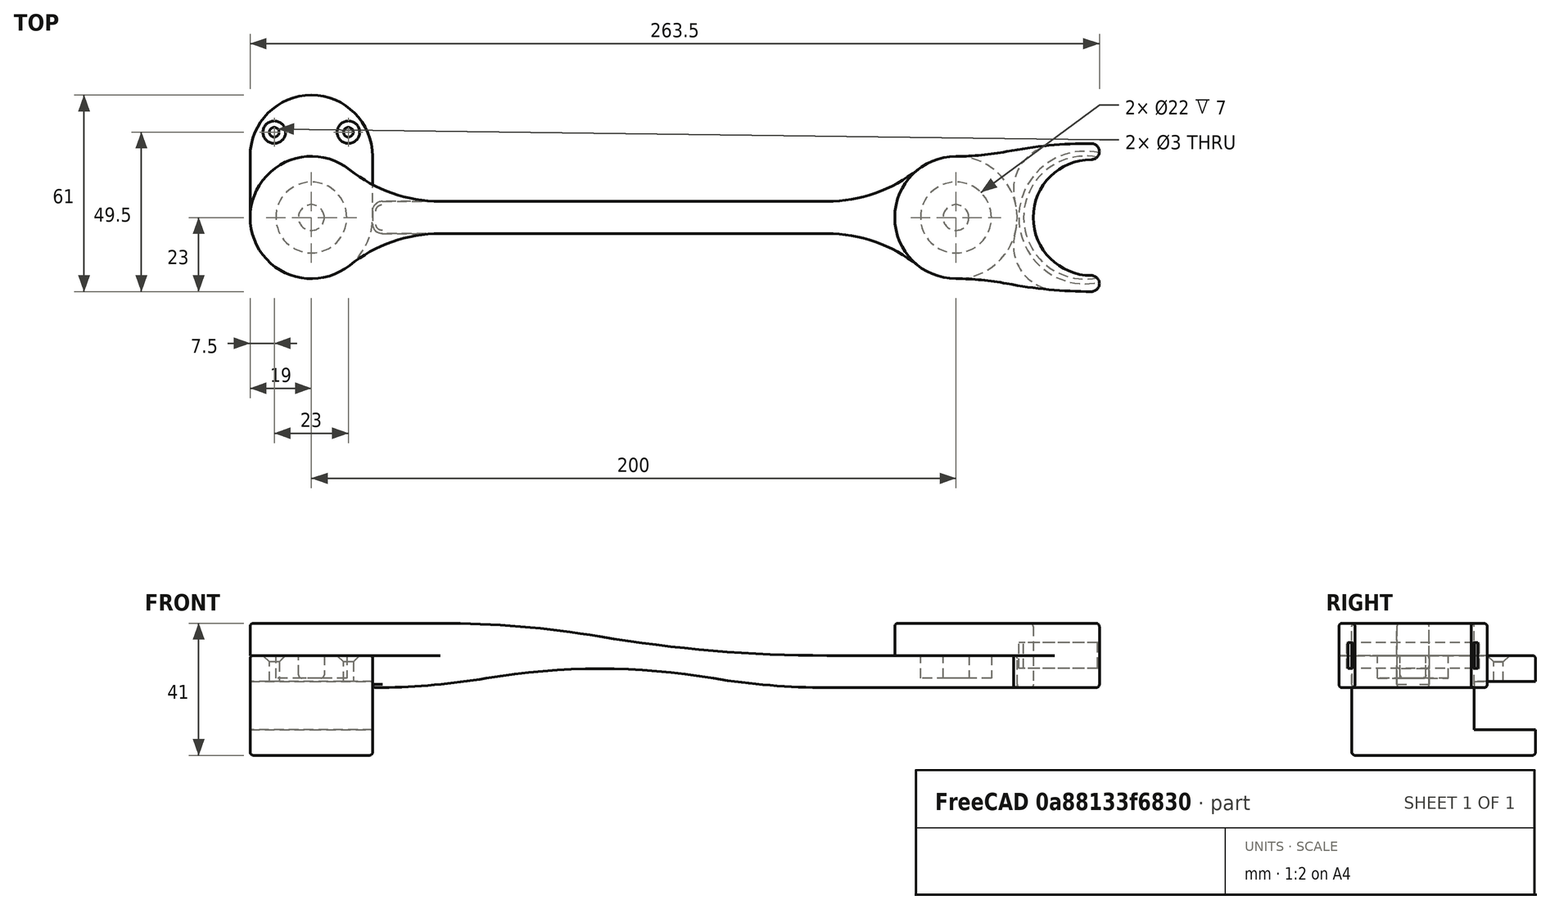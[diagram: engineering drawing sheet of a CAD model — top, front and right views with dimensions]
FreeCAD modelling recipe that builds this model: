
FCSTD DOCUMENT  (FreeCAD 0.21R33771 (Git))
Label: MicroscopeArm
License: All rights reserved
LicenseURL: http://en.wikipedia.org/wiki/All_rights_reserved
objects: Sketcher::SketchObject×13, PartDesign::Pad×7, PartDesign::Pocket×7, PartDesign::Fillet×6, PartDesign::Body×3, App::Part×3, Mesh::Feature×3, PartDesign::SubShapeBinder×2, Spreadsheet::Sheet×1
note: 58 computed .brp shape members not serialized (recipe doc carries the construction recipe); baked Part::Feature solids carry a one-line shape summary decoded from their .brp

FEATURE [Spreadsheet::Sheet] Spreadsheet
  cells = A1='HalfArmLength; B1(HalfArmLength)=200; A2='BearingOuterDiameter; B2(BearingOuterDiameter)=22; A3='BearingInnerDiameter; B3(BearingInnerDiameter)=8; A4='TableThickness; B4(TableThickness)=15; A5='Wall; B5(Wall)=8; A6='BearingThickness; B6(BearingThickness)=7; A7='ScrewHeadDiameter; B7(ScrewHeadDiameter)=7; A8='ScrewDiameter; B8(ScrewDiameter)=3; A9='ArmThickness; B9(ArmThickness)=38; A10='ArmThinness; B10(ArmThinness)=10; A11='ArmTransitionSize; B11(ArmTransitionSize)=40; A12='MicroscopeDiameter; B12(MicroscopeDiameter)=36
FEATURE [Sketcher::SketchObject] Sketch  label="TableAttachmentTopSketch"
  FullyConstrained = true
  MapMode = 5
  Support = -> [XY_Plane001]
  expr: Constraints[2] = Spreadsheet.Wall * 2 + Spreadsheet.BearingOuterDiameter
  expr: Constraints[8] = Spreadsheet.Wall + Spreadsheet.BearingOuterDiameter / 2
  sketch-geometry (5):
    g0: ArcOfCircle CenterX=0 CenterY=0 CenterZ=0 NormalX=0 NormalY=0 NormalZ=1 AngleXU=0 Radius=19 StartAngle=3.14159 EndAngle=6.28319
    g1: LineSegment StartX=-19 StartY=2.3e-15 StartZ=0 EndX=-19 EndY=19 EndZ=0
    g2: LineSegment StartX=19 StartY=-4.7e-15 StartZ=0 EndX=19 EndY=19 EndZ=0
    g3: LineSegment StartX=-19 StartY=19 StartZ=0 EndX=0 EndY=19 EndZ=0
    g4: ArcOfCircle CenterX=1.1e-15 CenterY=19 CenterZ=0 NormalX=0 NormalY=0 NormalZ=1 AngleXU=0 Radius=19 StartAngle=0 EndAngle=3.14159
  constraints (15):
    c: PointOnObject(g0,g-1)
    c: PointOnObject(g0,g-1)
    c: Diameter(g0) = 38
    c: Coincident(g1,g0)
    c: Vertical(g1)
    c: Coincident(g2,g0)
    c: Vertical(g2)
    c: Horizontal(g1,g2)
    c: DistanceY(g1,g1) = 19
    c: Coincident(g3,g1)
    c: Horizontal(g3)
    c: Coincident(g4,g3)
    c: Coincident(g4,g1)
    c: Coincident(g4,g2)
    c: Coincident(g0,g-1)
FEATURE [PartDesign::Pad] Pad  label="TableAttachmentTopPad"
  Direction = (0,0,1)
  Length = 31
  Length2 = 10
  Profile = -> Sketch
  ReferenceAxis = -> Sketch [N_Axis]
  Type = 0
  expr: Length = Spreadsheet.TableThickness + 2 * Spreadsheet.Wall
FEATURE [Sketcher::SketchObject] Sketch001  label="TableCutSketch"
  ExternalGeometry = -> [Pad]
  FullyConstrained = true
  MapMode = 5
  Placement = pos=(0,0,0) rot=(0.57735,0.57735,0.57735;2.0944rad)
  Support = -> [YZ_Plane001]
  expr: Constraints[8] = Spreadsheet.TableThickness
  expr: Constraints[9] = Spreadsheet.Wall
  sketch-geometry (4):
    g0: LineSegment StartX=38 StartY=23 StartZ=0 EndX=19 EndY=23 EndZ=0
    g1: LineSegment StartX=19 StartY=23 StartZ=0 EndX=19 EndY=8 EndZ=0
    g2: LineSegment StartX=19 StartY=8 StartZ=0 EndX=38 EndY=8 EndZ=0
    g3: LineSegment StartX=38 StartY=8 StartZ=0 EndX=38 EndY=23 EndZ=0
  constraints (12):
    c: Coincident(g0,g1)
    c: Coincident(g1,g2)
    c: Coincident(g2,g3)
    c: Coincident(g3,g0)
    c: Horizontal(g0)
    c: Horizontal(g2)
    c: Vertical(g1)
    c: Vertical(g3)
    c: DistanceY(g3,g3) = 15
    c: DistanceY(g-1,g2) = 8
    c: Vertical(g0,g-3)
    c: Vertical(g-3,g0)
FEATURE [PartDesign::Pocket] Pocket  label="TableCut"
  BaseFeature = -> Pad
  Direction = (-1,2e-16,-3e-16)
  Length = 38
  Length2 = 5
  Midplane = true
  Profile = -> Sketch001
  ReferenceAxis = -> Sketch001 [N_Axis]
  Type = 0
  expr: Length = Spreadsheet.BearingOuterDiameter + 2 * Spreadsheet.Wall
FEATURE [Sketcher::SketchObject] Sketch002  label="BearingPocketSketch"
  FullyConstrained = true
  MapMode = 5
  Placement = pos=(0,0,31) rot=(0,0,1;0rad)
  Support = -> [Pocket]
  expr: Constraints[1] = Spreadsheet.BearingOuterDiameter
  sketch-geometry (1):
    g0: Circle CenterX=0 CenterY=0 CenterZ=0 NormalX=0 NormalY=0 NormalZ=1 AngleXU=0 Radius=11
  constraints (2):
    c: Coincident(g0,g-1)
    c: Diameter(g0) = 22
FEATURE [PartDesign::Pocket] Pocket001  label="BearingPocket"
  BaseFeature = -> Pocket
  Direction = (0,0,-1)
  Length = 7
  Length2 = 5
  Profile = -> Sketch002
  ReferenceAxis = -> Sketch002 [N_Axis]
  Type = 0
  expr: Length = Spreadsheet.BearingThickness
FEATURE [Sketcher::SketchObject] Sketch003  label="ScrewHeadPocketSketch"
  ExternalGeometry = -> [Pocket001]
  FullyConstrained = true
  MapMode = 5
  Placement = pos=(0,0,31) rot=(0,0,1;0rad)
  Support = -> [Pocket001]
  expr: Constraints[11] = Spreadsheet.ScrewHeadDiameter / 2 + Spreadsheet.Wall / 2
  expr: Constraints[8] = Spreadsheet.ScrewHeadDiameter
  expr: Constraints[9] = Spreadsheet.ScrewHeadDiameter / 2 + Spreadsheet.Wall / 2
  sketch-geometry (5):
    g0: Circle CenterX=-11.5 CenterY=26.5 CenterZ=0 NormalX=0 NormalY=0 NormalZ=1 AngleXU=0 Radius=3.5
    g1: Circle CenterX=11.5 CenterY=26.5 CenterZ=0 NormalX=0 NormalY=0 NormalZ=1 AngleXU=0 Radius=3.5
    g2: LineSegment StartX=-19 StartY=19 StartZ=0 EndX=19 EndY=19 EndZ=0
    g3: LineSegment StartX=-11.5 StartY=26.5 StartZ=0 EndX=1.8e-15 EndY=19 EndZ=0
    g4: LineSegment StartX=1.8e-15 StartY=19 StartZ=0 EndX=11.5 EndY=26.5 EndZ=0
  constraints (12):
    c: Coincident(g2,g-3)
    c: Coincident(g2,g-3)
    c: Equal(g1,g0)
    c: Coincident(g3,g0)
    c: Coincident(g3,g-3)
    c: Coincident(g4,g3)
    c: Coincident(g4,g1)
    c: Equal(g3,g4)
    c: Diameter(g0) = 7
    c: DistanceX(g1,g2) = 7.5
    c: Horizontal(g1,g0)
    c: DistanceY(g2,g1) = 7.5
FEATURE [PartDesign::Pocket] Pocket002  label="ScrewHeadPocket"
  BaseFeature = -> Pocket001
  Direction = (0,0,-1)
  Length = 2
  Length2 = 5
  Profile = -> Sketch003
  ReferenceAxis = -> Sketch003 [N_Axis]
  TaperAngle = -45
  Type = 0
  expr: Length = (Spreadsheet.ScrewHeadDiameter - Spreadsheet.ScrewDiameter) / 2
FEATURE [PartDesign::Pocket] Pocket003  label="ScrewPocket"
  BaseFeature = -> Pocket002
  Direction = (0,0,-1)
  Length = 6
  Length2 = 5
  Profile = -> Pocket002 [Edge31,Edge29]
  Type = 0
  expr: Length = Spreadsheet.Wall - (Spreadsheet.ScrewHeadDiameter - Spreadsheet.ScrewDiameter) / 2
FEATURE [PartDesign::Fillet] Fillet
  Base = -> Pocket003 [Face4]
  BaseFeature = -> Pocket003
  Radius = 1
  SupportTransform = false
  UseAllEdges = false
FEATURE [PartDesign::Fillet] Fillet001
  Base = -> Fillet [Edge3,Edge6,Edge14,Edge13]
  BaseFeature = -> Fillet
  Radius = 1
  SupportTransform = false
  UseAllEdges = false
FEATURE [PartDesign::Body] Body  label="TableAttachmentBody"
  Group = -> [Sketch,Pad,Sketch001,Pocket,Sketch002,Pocket001,Sketch003,Pocket002,Pocket003,Fillet,Fillet001]
  Origin = -> Origin001
  Tip = -> Fillet001
FEATURE [App::Part] Part  label="TableAttachment"
  Group = -> [Body]
  Origin = -> Origin
FEATURE [Mesh::Feature] Mesh  label="TableAttachment (Meshed)"
FEATURE [PartDesign::SubShapeBinder] Binder  label="TableAttachmentBearingPocketSketchBinder"
  BindCopyOnChange = 0
  BindMode = 0
  ClaimChildren = false
  Context = -> Part001 [Body001.Binder.]
  Fuse = false
  MakeFace = true
  OffsetFill = false
  OffsetIntersection = false
  OffsetJoinType = 0
  OffsetOpenResult = false
  PartialLoad = false
  Relative = true
  Support = -> [Part[Body.Pocket001.Sketch002.]]
  _Version = 2
FEATURE [Sketcher::SketchObject] Sketch004  label="ArmTopSketch"
  ExternalGeometry = -> [Binder]
  FullyConstrained = true
  MapMode = 5
  Placement = pos=(0,0,31) rot=(0,0,1;0rad)
  Support = -> [Binder]
  expr: Constraints[10] = <<Spreadsheet>>.ArmThinness
  expr: Constraints[11] = <<Spreadsheet>>.ArmTransitionSize
  expr: Constraints[15] = <<Spreadsheet>>.HalfArmLength - <<Spreadsheet>>.ArmThickness / 2
  expr: Constraints[1] = <<Spreadsheet>>.ArmThickness
  sketch-geometry (6):
    g0: ArcOfCircle CenterX=0 CenterY=0 CenterZ=0 NormalX=0 NormalY=0 NormalZ=1 AngleXU=0 Radius=19 StartAngle=0.897447 EndAngle=5.38574
    g1: LineSegment StartX=40 StartY=5 StartZ=0 EndX=181 EndY=5 EndZ=0
    g2: ArcOfCircle CenterX=40 CenterY=50.1429 CenterZ=0 NormalX=0 NormalY=0 NormalZ=1 AngleXU=0 Radius=45.1429 StartAngle=4.03904 EndAngle=4.71239
    g3: LineSegment StartX=40 StartY=-5 StartZ=0 EndX=181 EndY=-5 EndZ=0
    g4: ArcOfCircle CenterX=40 CenterY=-50.1429 CenterZ=0 NormalX=0 NormalY=0 NormalZ=1 AngleXU=0 Radius=45.1429 StartAngle=1.5708 EndAngle=2.24415
    g5: LineSegment StartX=181 StartY=5 StartZ=0 EndX=181 EndY=-5 EndZ=0
  constraints (16):
    c: Coincident(g0,g-3)
    c: Diameter(g0) = 38
    c: Vertical(g0,g0)
    c: Horizontal(g1)
    c: Tangent(g2,g1) = -1.5708
    c: Tangent(g2,g0) = 1.5708
    c: Horizontal(g3)
    c: Vertical(g1,g3)
    c: Tangent(g4,g3) = 1.5708
    c: Tangent(g4,g0) = 1.5708
    c: DistanceY(g3,g1) = 10
    c: DistanceX(g0,g1) = 40
    c: Vertical(g5)
    c: Coincident(g3,g5)
    c: Coincident(g1,g5)
    c: DistanceX(g0,g3) = 181
FEATURE [PartDesign::Pad] Pad001  label="ArmTopPad"
  Direction = (0,0,1)
  Length = 10
  Length2 = 10
  Profile = -> Sketch004
  ReferenceAxis = -> Sketch004 [N_Axis]
  Refine = true
  Type = 0
  expr: Length = <<Spreadsheet>>.ArmThinness
FEATURE [Sketcher::SketchObject] Sketch005  label="ArmUnderSketch"
  FullyConstrained = true
  MapMode = 5
  Placement = pos=(0,0,31) rot=(1,0,0;3.14159rad)
  Support = -> [Pad001]
  expr: Constraints[10] = <<Spreadsheet>>.HalfArmLength
  expr: Constraints[12] = <<Spreadsheet>>.ArmTransitionSize
  expr: Constraints[4] = <<Spreadsheet>>.ArmThinness
  expr: Constraints[5] = <<Spreadsheet>>.ArmThickness / 2
  expr: Constraints[9] = <<Spreadsheet>>.ArmThickness
  sketch-geometry (6):
    g0: LineSegment StartX=19 StartY=5 StartZ=0 EndX=160 EndY=5 EndZ=0
    g1: LineSegment StartX=160 StartY=-5 StartZ=0 EndX=19 EndY=-5 EndZ=0
    g2: LineSegment StartX=19 StartY=-5 StartZ=0 EndX=19 EndY=5 EndZ=0
    g3: ArcOfCircle CenterX=200 CenterY=0 CenterZ=0 NormalX=0 NormalY=0 NormalZ=1 AngleXU=0 Radius=19 StartAngle=4.03904 EndAngle=8.52733
    g4: ArcOfCircle CenterX=160 CenterY=50.1429 CenterZ=0 NormalX=0 NormalY=0 NormalZ=1 AngleXU=0 Radius=45.1429 StartAngle=4.71239 EndAngle=5.38574
    g5: ArcOfCircle CenterX=160 CenterY=-50.1429 CenterZ=0 NormalX=0 NormalY=0 NormalZ=1 AngleXU=0 Radius=45.1429 StartAngle=0.897447 EndAngle=1.5708
  constraints (16):
    c: Coincident(g1,g2)
    c: Coincident(g2,g0)
    c: Horizontal(g0)
    c: Horizontal(g1)
    c: DistanceY(g2,g2) = 10
    c: DistanceX(g-1,g0) = 19
    c: Symmetric(g0,g1,g-1)
    c: PointOnObject(g3,g-1)
    c: Vertical(g3,g3)
    c: Diameter(g3) = 38
    c: DistanceX(g-1,g3) = 200
    c: Tangent(g4,g3) = 1.5708
    c: DistanceX(g4,g3) = 40
    c: Tangent(g5,g3) = 1.5708
    c: Tangent(g5,g1) = -1.5708
    c: Tangent(g0,g4) = -1.5708
FEATURE [PartDesign::Pad] Pad002  label="ArmUnderPad"
  BaseFeature = -> Pad001
  Direction = (0,0,-1)
  Length = 10
  Length2 = 10
  Profile = -> Sketch005
  ReferenceAxis = -> Sketch005 [N_Axis]
  Refine = true
  Type = 0
  expr: Length = <<Spreadsheet>>.ArmThinness
FEATURE [Sketcher::SketchObject] Sketch006
  ExternalGeometry = -> [Pad002]
  FullyConstrained = true
  MapMode = 5
  Placement = pos=(0,0,31) rot=(0,0,1;0rad)
  Support = -> [Pad002]
  expr: Constraints[1] = <<Spreadsheet>>.BearingOuterDiameter
  sketch-geometry (1):
    g0: Circle CenterX=200 CenterY=0 CenterZ=0 NormalX=0 NormalY=0 NormalZ=1 AngleXU=0 Radius=11
  constraints (2):
    c: Coincident(g0,g-3)
    c: Diameter(g0) = 22
FEATURE [PartDesign::Pocket] Pocket004
  BaseFeature = -> Pad002
  Direction = (0,0,-1)
  Length = 7
  Length2 = 5
  Profile = -> Sketch006
  ReferenceAxis = -> Sketch006 [N_Axis]
  Type = 0
  expr: Length = <<Spreadsheet>>.BearingThickness
FEATURE [Sketcher::SketchObject] Sketch007  label="BearingPegSketch"
  ExternalGeometry = -> [Pocket004]
  FullyConstrained = true
  MapMode = 5
  Placement = pos=(0,0,31) rot=(1,0,0;3.14159rad)
  Support = -> [Pocket004]
  expr: Constraints[1] = <<Spreadsheet>>.BearingInnerDiameter
  sketch-geometry (1):
    g0: Circle CenterX=0 CenterY=0 CenterZ=0 NormalX=0 NormalY=0 NormalZ=1 AngleXU=0 Radius=4
  constraints (2):
    c: Coincident(g0,g-3)
    c: Diameter(g0) = 8
FEATURE [PartDesign::Pad] Pad003  label="BearingPeg"
  BaseFeature = -> Pocket004
  Direction = (0,0,-1)
  Length = 7
  Length2 = 10
  Profile = -> Sketch007
  ReferenceAxis = -> Sketch007 [N_Axis]
  Type = 0
  expr: Length = <<Spreadsheet>>.BearingThickness
FEATURE [Sketcher::SketchObject] Sketch008  label="ArchSketch"
  ExternalGeometry = -> [Pad003]
  FullyConstrained = true
  MapMode = 5
  Placement = pos=(0,-5,1.7e-15) rot=(1,0,0;1.5708rad)
  Support = -> [Pad003]
  expr: Constraints[15] = <<Spreadsheet>>.ArmThinness
  sketch-geometry (11):
    g0: GeomPoint X=89.5 Y=21 Z=0
    g1: ArcOfCircle CenterX=40 CenterY=-258.063 CenterZ=0 NormalX=0 NormalY=0 NormalZ=1 AngleXU=0 Radius=299.063 StartAngle=1.40451 EndAngle=1.5708
    g2: ArcOfCircle CenterX=160 CenterY=456.938 CenterZ=0 NormalX=0 NormalY=0 NormalZ=1 AngleXU=0 Radius=425.938 StartAngle=4.54611 EndAngle=4.71239
    g3: LineSegment StartX=160 StartY=31 StartZ=0 EndX=188.151 EndY=31 EndZ=0
    g4: LineSegment StartX=188.151 StartY=31 StartZ=0 EndX=188.151 EndY=41 EndZ=0
    g5: LineSegment StartX=188.151 StartY=41 StartZ=0 EndX=40 EndY=41 EndZ=0
    g6: ArcOfCircle CenterX=19 CenterY=233.969 CenterZ=0 NormalX=0 NormalY=0 NormalZ=1 AngleXU=0 Radius=212.969 StartAngle=4.71239 EndAngle=4.87867
    g7: ArcOfCircle CenterX=89.5 CenterY=-186.094 CenterZ=0 NormalX=0 NormalY=0 NormalZ=1 AngleXU=0 Radius=212.969 StartAngle=1.40451 EndAngle=1.73708
    g8: ArcOfCircle CenterX=160 CenterY=233.969 CenterZ=0 NormalX=0 NormalY=0 NormalZ=1 AngleXU=0 Radius=212.969 StartAngle=4.54611 EndAngle=4.71239
    g9: GeomPoint X=89.5 Y=26.875 Z=0
    g10: LineSegment StartX=19 StartY=21 StartZ=0 EndX=160 EndY=21 EndZ=0
  constraints (25):
    c: Tangent(g2,g-4) = -1.5708
    c: Tangent(g2,g1) = 1.5708
    c: Coincident(g3,g2)
    c: Coincident(g3,g-4)
    c: Vertical(g4)
    c: Coincident(g5,g4)
    c: Horizontal(g5)
    c: Tangent(g1,g-3) = -1.5708
    c: Coincident(g4,g3)
    c: Coincident(g5,g1)
    c: Vertical(g1,g0)
    c: Horizontal(g6,g7)
    c: Tangent(g7,g6) = 1.5708
    c: Tangent(g8,g7) = 1.5708
    c: PointOnObject(g9,g7)
    c: DistanceY(g9,g1) = 10
    c: Symmetric(g9,g8,g7)
    c: Coincident(g10,g6)
    c: Coincident(g10,g8)
    c: Horizontal(g10)
    c: Symmetric(g6,g8,g0)
    c: Vertical(g2,g8)
    c: Vertical(g9,g0)
    c: Coincident(g-5,g6)
    c: Vertical(g7,g0)
FEATURE [PartDesign::Pocket] Pocket005  label="ArchPocket"
  BaseFeature = -> Pad003
  Direction = (0,1,-4e-16)
  Length = 5
  Length2 = 5
  Profile = -> Sketch008
  ReferenceAxis = -> Sketch008 [N_Axis]
  Refine = true
  Type = 1
FEATURE [PartDesign::Fillet] Fillet002  label="BearingPegFillet"
  Base = -> Pocket005 [Edge40]
  BaseFeature = -> Pocket005
  Radius = 1
  SupportTransform = false
  UseAllEdges = false
FEATURE [PartDesign::Fillet] Fillet003  label="EndOfArchFillet"
  Base = -> Fillet002 [Edge17,Edge26]
  BaseFeature = -> Fillet002
  Radius = 3
  SupportTransform = false
  UseAllEdges = false
FEATURE [PartDesign::Fillet] Fillet004  label="TopAndBottomFillets"
  Base = -> Fillet003 [Edge54,Edge25]
  BaseFeature = -> Fillet003
  Radius = 1
  SupportTransform = false
  UseAllEdges = false
FEATURE [PartDesign::Body] Body001  label="ArmBody"
  Group = -> [Binder,Sketch004,Pad001,Sketch005,Pad002,Sketch006,Pocket004,Sketch007,Pad003,Sketch008,Pocket005,Fillet002,Fillet003,Fillet004]
  Origin = -> Origin003
  Tip = -> Fillet004
FEATURE [App::Part] Part001  label="Arm"
  Group = -> [Body001]
  Origin = -> Origin002
FEATURE [Mesh::Feature] Mesh001  label="Arm (Meshed)"
FEATURE [PartDesign::SubShapeBinder] Binder001  label="ArmUnderSketchBinder"
  BindCopyOnChange = 0
  BindMode = 0
  ClaimChildren = false
  Context = -> Part002 [Body002.Binder001.]
  Fuse = false
  MakeFace = true
  OffsetFill = false
  OffsetIntersection = false
  OffsetJoinType = 0
  OffsetOpenResult = false
  PartialLoad = false
  Relative = true
  Support = -> [Part001[Body001.Pad002.Sketch005.]]
  _Version = 2
FEATURE [Sketcher::SketchObject] Sketch009  label="HolderSketch"
  ExternalGeometry = -> [Binder001]
  FullyConstrained = true
  MapMode = 5
  Placement = pos=(0,0,31) rot=(0,0,1;0rad)
  Support = -> [Binder001]
  expr: Constraints[5] = <<Spreadsheet>>.MicroscopeDiameter
  expr: Constraints[6] = (<<Spreadsheet>>.MicroscopeDiameter + <<Spreadsheet>>.ArmThickness) / 2 + 5
  sketch-geometry (8):
    g0: ArcOfCircle CenterX=200 CenterY=0 CenterZ=0 NormalX=0 NormalY=0 NormalZ=1 AngleXU=0 Radius=19 StartAngle=1.5708 EndAngle=4.71239
    g1: ArcOfCircle CenterX=242 CenterY=0 CenterZ=0 NormalX=0 NormalY=0 NormalZ=1 AngleXU=0 Radius=18 StartAngle=1.5708 EndAngle=4.71239
    g2: ArcOfCircle CenterX=242 CenterY=20.5 CenterZ=0 NormalX=0 NormalY=0 NormalZ=1 AngleXU=0 Radius=2.5 StartAngle=4.71239 EndAngle=7.85398
    g3: ArcOfCircle CenterX=242 CenterY=-116.063 CenterZ=0 NormalX=0 NormalY=0 NormalZ=1 AngleXU=0 Radius=139.063 StartAngle=1.5708 EndAngle=1.7607
    g4: ArcOfCircle CenterX=200 CenterY=102.438 CenterZ=0 NormalX=0 NormalY=0 NormalZ=1 AngleXU=0 Radius=83.4375 StartAngle=4.71239 EndAngle=4.90229
    g5: ArcOfCircle CenterX=200 CenterY=-102.438 CenterZ=0 NormalX=0 NormalY=0 NormalZ=1 AngleXU=0 Radius=83.4375 StartAngle=1.38089 EndAngle=1.5708
    g6: ArcOfCircle CenterX=242 CenterY=116.063 CenterZ=0 NormalX=0 NormalY=0 NormalZ=1 AngleXU=0 Radius=139.063 StartAngle=4.52249 EndAngle=4.71239
    g7: ArcOfCircle CenterX=242 CenterY=-20.5 CenterZ=0 NormalX=0 NormalY=0 NormalZ=1 AngleXU=0 Radius=2.5 StartAngle=4.71239 EndAngle=7.85398
  constraints (23):
    c: Coincident(g0,g-3)
    c: PointOnObject(g0,g-3)
    c: Vertical(g0,g0)
    c: PointOnObject(g1,g-1)
    c: Vertical(g1,g1)
    c: Diameter(g1) = 36
    c: DistanceX(g0,g1) = 42
    c: Vertical(g1,g1)
    c: Vertical(g0,g0)
    c: Tangent(g1,g2) = 1.5708
    c: Tangent(g2,g3) = -1.5708
    c: Tangent(g3,g4) = 1.5708
    c: Tangent(g4,g0) = 1.5708
    c: Vertical(g2,g1)
    c: DistanceY(g1,g2) = 5
    c: Horizontal(g3,g2)
    c: Tangent(g0,g5) = 1.5708
    c: Tangent(g5,g6) = 1.5708
    c: Tangent(g6,g7) = -1.5708
    c: Vertical(g6,g1)
    c: Horizontal(g5,g7)
    c: Tangent(g7,g1) = 1.5708
    c: DistanceY(g6,g1) = 5
FEATURE [PartDesign::Pad] Pad004  label="HolderPad"
  Direction = (0,0,1)
  Length = 10
  Length2 = 10
  Profile = -> Sketch009
  ReferenceAxis = -> Sketch009 [N_Axis]
  Type = 0
  expr: Length = <<Spreadsheet>>.ArmThinness
FEATURE [Sketcher::SketchObject] Sketch010  label="BearingConnectorSketch"
  ExternalGeometry = -> [Pad004]
  FullyConstrained = true
  MapMode = 5
  Placement = pos=(0,0,31) rot=(1,0,0;3.14159rad)
  Support = -> [Pad004]
  expr: Constraints[1] = <<Spreadsheet>>.BearingInnerDiameter
  sketch-geometry (1):
    g0: Circle CenterX=200 CenterY=0 CenterZ=0 NormalX=0 NormalY=0 NormalZ=1 AngleXU=0 Radius=4
  constraints (2):
    c: Coincident(g0,g-3)
    c: Diameter(g0) = 8
FEATURE [PartDesign::Pad] Pad005  label="BearingConnectorPad"
  BaseFeature = -> Pad004
  Direction = (0,0,-1)
  Length = 7
  Length2 = 10
  Profile = -> Sketch010
  ReferenceAxis = -> Sketch010 [N_Axis]
  Type = 0
  expr: Length = <<Spreadsheet>>.BearingThickness
FEATURE [Sketcher::SketchObject] Sketch011  label="StrapSketch"
  AttachmentOffset = pos=(0,0,-10) rot=(0,0,1;0rad)
  ExternalGeometry = -> [Pad005]
  FullyConstrained = true
  MapMode = 5
  Placement = pos=(0,0,31) rot=(0,0,1;0rad)
  Support = -> [Pad005]
  expr: .AttachmentOffset.Base.z = -<<Spreadsheet>>.ArmThinness
  sketch-geometry (6):
    g0: Circle CenterX=240.089 CenterY=0 CenterZ=0 NormalX=0 NormalY=0 NormalZ=1 AngleXU=0 Radius=19.0889
    g1: Circle CenterX=240.089 CenterY=0 CenterZ=0 NormalX=0 NormalY=0 NormalZ=1 AngleXU=0 Radius=20.5889
    g2: GeomPoint X=259.178 Y=0 Z=0
    g3: GeomPoint X=260.678 Y=0 Z=0
    g4: GeomPoint X=221 Y=0 Z=0
    g5: GeomPoint X=224 Y=0 Z=0
  constraints (13):
    c: PointOnObject(g0,g-1)
    c: PointOnObject(g2,g0)
    c: PointOnObject(g3,g1)
    c: PointOnObject(g3,g-1)
    c: PointOnObject(g2,g-1)
    c: DistanceX(g2,g3) = 1.5
    c: PointOnObject(g4,g0)
    c: PointOnObject(g4,g-1)
    c: PointOnObject(g-3,g1)
    c: Coincident(g0,g1)
    c: PointOnObject(g5,g-4)
    c: PointOnObject(g5,g-1)
    c: DistanceX(g4,g5) = 3
FEATURE [Sketcher::SketchObject] Sketch012  label="UndersideSketch"
  ExternalGeometry = -> [Pad005]
  FullyConstrained = true
  MapMode = 5
  Placement = pos=(0,0,31) rot=(1,0,0;3.14159rad)
  Support = -> [Pad005]
  sketch-geometry (8):
    g0: ArcOfCircle CenterX=200 CenterY=0 CenterZ=0 NormalX=0 NormalY=0 NormalZ=1 AngleXU=0 Radius=19 StartAngle=6.01689 EndAngle=6.54948
    g1: ArcOfCircle CenterX=242 CenterY=0 CenterZ=0 NormalX=0 NormalY=0 NormalZ=1 AngleXU=0 Radius=18 StartAngle=1.5708 EndAngle=4.71239
    g2: ArcOfCircle CenterX=242 CenterY=-20.5 CenterZ=0 NormalX=0 NormalY=0 NormalZ=1 AngleXU=0 Radius=2.5 StartAngle=4.71239 EndAngle=7.85398
    g3: ArcOfCircle CenterX=231.757 CenterY=-8.66253 CenterZ=0 NormalX=0 NormalY=0 NormalZ=1 AngleXU=0 Radius=13.9176 StartAngle=2.8753 EndAngle=4.63045
    g4: ArcOfCircle CenterX=231.757 CenterY=8.66253 CenterZ=0 NormalX=0 NormalY=0 NormalZ=1 AngleXU=0 Radius=13.9176 StartAngle=1.65273 EndAngle=3.40789
    g5: ArcOfCircle CenterX=242 CenterY=116.063 CenterZ=0 NormalX=0 NormalY=0 NormalZ=1 AngleXU=0 Radius=139.063 StartAngle=4.63045 EndAngle=4.71239
    g6: ArcOfCircle CenterX=242 CenterY=20.5 CenterZ=0 NormalX=0 NormalY=0 NormalZ=1 AngleXU=0 Radius=2.5 StartAngle=4.71239 EndAngle=7.85398
    g7: ArcOfCircle CenterX=242 CenterY=-116.063 CenterZ=0 NormalX=0 NormalY=0 NormalZ=1 AngleXU=0 Radius=139.063 StartAngle=1.5708 EndAngle=1.65273
  constraints (22):
    c: Equal(g-3,g0)
    c: Coincident(g0,g-3)
    c: Coincident(g5,g-8)
    c: Coincident(g1,g-4)
    c: Coincident(g1,g-5)
    c: Tangent(g4,g-6) = -1.5708
    c: DistanceY(g0,g0) = 10
    c: Vertical(g0,g0)
    c: Tangent(g4,g0) = 1.5708
    c: Tangent(g3,g-8) = -1.5708
    c: Tangent(g3,g0) = 1.5708
    c: Vertical(g1,g1)
    c: Coincident(g2,g1)
    c: Coincident(g-7,g2)
    c: Coincident(g5,g3)
    c: Coincident(g2,g5)
    c: Coincident(g6,g-5)
    c: Coincident(g6,g1)
    c: Vertical(g6,g6)
    c: Coincident(g-6,g7)
    c: Coincident(g7,g4)
    c: Vertical(g7,g6)
FEATURE [PartDesign::Pad] Pad006  label="UndersidePad"
  BaseFeature = -> Pad005
  Direction = (0,0,-1)
  Length = 10
  Length2 = 10
  Profile = -> Sketch012
  ReferenceAxis = -> Sketch012 [N_Axis]
  Refine = true
  Type = 0
  expr: Length = <<Spreadsheet>>.ArmThinness
FEATURE [PartDesign::Pocket] Pocket006  label="StrapPocket"
  BaseFeature = -> Pad006
  Direction = (0,0,-1)
  Length = 8
  Length2 = 5
  Midplane = true
  Profile = -> Sketch011
  ReferenceAxis = -> Sketch011 [N_Axis]
  Type = 0
FEATURE [PartDesign::Fillet] Fillet005  label="TopAndBottomFillet"
  Base = -> Pocket006 [Edge38,Edge4]
  BaseFeature = -> Pocket006
  Radius = 1
  SupportTransform = false
  UseAllEdges = false
FEATURE [PartDesign::Body] Body002  label="MicroscopeHolderBody"
  Group = -> [Binder001,Sketch009,Pad004,Sketch010,Pad005,Sketch011,Sketch012,Pad006,Pocket006,Fillet005]
  Origin = -> Origin005
  Tip = -> Fillet005
FEATURE [App::Part] Part002  label="MicroscopeHolder"
  Group = -> [Body002]
  Origin = -> Origin004
FEATURE [Mesh::Feature] Mesh002  label="MicroscopeHolderBody (Meshed)"
